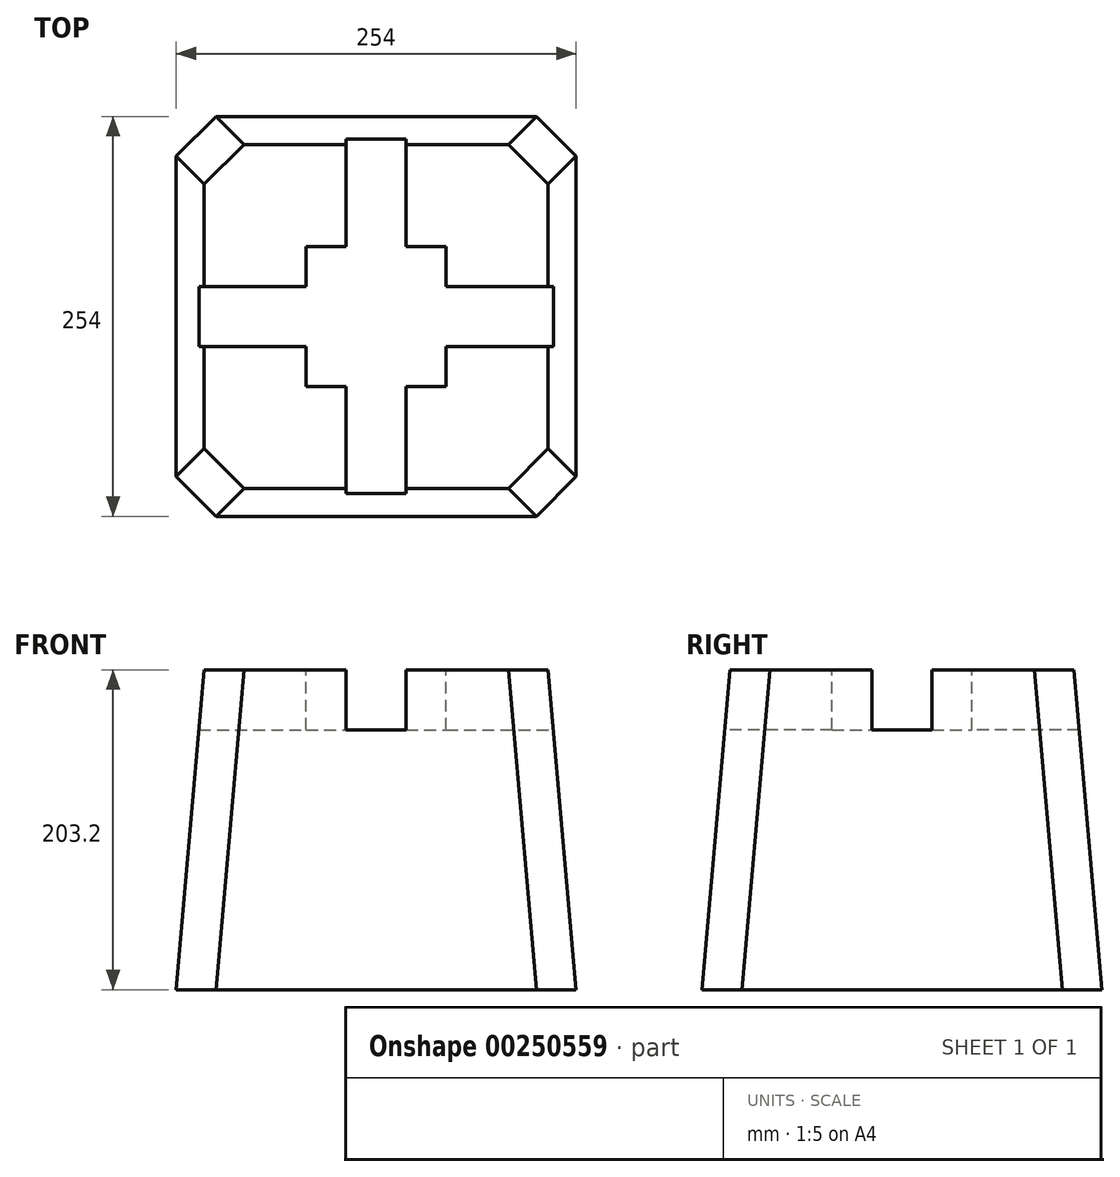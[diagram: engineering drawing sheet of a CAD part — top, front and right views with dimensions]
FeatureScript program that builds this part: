
annotation { "Feature Type Name" : "Feature", "Feature Type Description" : "" }
export const myFeature = defineFeature(function(context is Context, id is Id, definition is map)
    precondition{}
    {
        {
            var Q0;
            Q0=qCreatedBy(makeId("Top.planeOp"),FACE);
            var sketch = newSketch(context, id + "F0", { "sketchPlane" : qUnion([Q0])});
            skLineSegment(sketch, "E0.bottom", {"start": v(-127, -127) * mm, "end": v(127, -127) * mm});
            skLineSegment(sketch, "E0.top", {"start": v(-127, 127) * mm, "end": v(127, 127) * mm});
            skLineSegment(sketch, "E0.left", {"start": v(-127, -127) * mm, "end": v(-127, 127) * mm});
            skLineSegment(sketch, "E0.right", {"start": v(127, -127) * mm, "end": v(127, 127) * mm});
            skSolve(sketch);
        }
        {
            var Q0;
            Q0 = qSketchRegion(id + "F0", true);
            extrude(context, id + "F1", {"entities" : qUnion([Q0]), "depth" : 203.2 * mm, "hasDraft" : true, "draftAngle" : 5 * degree, "draftPullDirection" : true});
        }
        {
            var Q0;
            Q0=makeQuery(id+"F1.opExtrude","SWEPT_EDGE",EDGE,{"disambiguationData":[OSD([sQuery(id+"F0.wireOp",EDGE,"E0.bottom"),sQuery(id+"F0.wireOp",EDGE,"E0.left")])]});
            var Q1;
            Q1=makeQuery(id+"F1.opExtrude","SWEPT_EDGE",EDGE,{"disambiguationData":[OSD([sQuery(id+"F0.wireOp",EDGE,"E0.bottom"),sQuery(id+"F0.wireOp",EDGE,"E0.right")])]});
            var Q2;
            Q2=makeQuery(id+"F1.opExtrude","SWEPT_EDGE",EDGE,{"disambiguationData":[OSD([sQuery(id+"F0.wireOp",EDGE,"E0.top"),sQuery(id+"F0.wireOp",EDGE,"E0.right")])]});
            var Q3;
            Q3=makeQuery(id+"F1.opExtrude","SWEPT_EDGE",EDGE,{"disambiguationData":[OSD([sQuery(id+"F0.wireOp",EDGE,"E0.top"),sQuery(id+"F0.wireOp",EDGE,"E0.left")])]});
            chamfer(context, id + "F2", {"entities" : qUnion([Q0, Q1, Q2, Q3]), "width" : 25.4 * mm, "tangentPropagation" : true});
        }
        {
            var Q0;
            Q0=makeQuery(id+"F1.opExtrude","CAP_FACE",FACE,{"disambiguationData":[OSD([sQuery(id+"F0.wireOp",EDGE,"E0.bottom"),sQuery(id+"F0.wireOp",EDGE,"E0.top"),sQuery(id+"F0.wireOp",EDGE,"E0.left"),sQuery(id+"F0.wireOp",EDGE,"E0.right")])],"isStart":false});
            var sketch = newSketch(context, id + "F3", { "sketchPlane" : qUnion([Q0])});
            skLineSegment(sketch, "E1", {"start": v(0, 109.22) * mm, "end": v(0, -109.22) * mm, "construction": true});
            skLineSegment(sketch, "E2", {"start": v(-109.22, 0) * mm, "end": v(109.22, 0) * mm, "construction": true});
            skLineSegment(sketch, "E3.0", {"start": v(19.05, 132.02) * mm, "end": v(19.05, 44.45) * mm});
            skLineSegment(sketch, "E4.0", {"start": v(-19.05, 132.02) * mm, "end": v(-19.05, 44.45) * mm});
            skLineSegment(sketch, "E5.0", {"start": v(-137.83, -19.05) * mm, "end": v(-44.45, -19.05) * mm});
            skLineSegment(sketch, "E6.0", {"start": v(-137.83, 19.05) * mm, "end": v(-44.45, 19.05) * mm});
            skLineSegment(sketch, "E7.trimOffspring", {"start": v(-19.05, -44.45) * mm, "end": v(-19.05, -130.36) * mm});
            skLineSegment(sketch, "E8.trimOffspring", {"start": v(44.45, 19.05) * mm, "end": v(136.5, 19.05) * mm});
            skLineSegment(sketch, "E9.trimOffspring", {"start": v(19.05, -44.45) * mm, "end": v(19.05, -130.36) * mm});
            skLineSegment(sketch, "E10.trimOffspring", {"start": v(44.45, -19.05) * mm, "end": v(136.5, -19.05) * mm});
            skLineSegment(sketch, "E11.bottom", {"start": v(-44.45, -44.45) * mm, "end": v(-19.05, -44.45) * mm});
            skLineSegment(sketch, "E11.top", {"start": v(-44.45, 44.45) * mm, "end": v(-19.05, 44.45) * mm});
            skLineSegment(sketch, "E11.left", {"start": v(-44.45, -44.45) * mm, "end": v(-44.45, -19.05) * mm});
            skLineSegment(sketch, "E11.right", {"start": v(44.45, -44.45) * mm, "end": v(44.45, -19.05) * mm});
            skLineSegment(sketch, "E12.trimOffspring", {"start": v(19.05, 44.45) * mm, "end": v(44.45, 44.45) * mm});
            skLineSegment(sketch, "E13.trimOffspring", {"start": v(44.45, 19.05) * mm, "end": v(44.45, 44.45) * mm});
            skLineSegment(sketch, "E14.trimOffspring", {"start": v(19.05, -44.45) * mm, "end": v(44.45, -44.45) * mm});
            skLineSegment(sketch, "E15.trimOffspring", {"start": v(-44.45, 19.05) * mm, "end": v(-44.45, 44.45) * mm});
            skLineSegment(sketch, "E16", {"start": v(-19.05, -130.36) * mm, "end": v(19.05, -130.36) * mm});
            skLineSegment(sketch, "E17", {"start": v(-137.83, -19.05) * mm, "end": v(-137.83, 19.05) * mm});
            skLineSegment(sketch, "E18", {"start": v(-19.05, 132.02) * mm, "end": v(19.05, 132.02) * mm});
            skLineSegment(sketch, "E19", {"start": v(136.5, 19.05) * mm, "end": v(136.5, -19.05) * mm});
            skPoint(sketch, "E20.orphan", {"position": v(-19.05, 104.78) * mm});
            skPoint(sketch, "E21.orphan", {"position": v(19.05, 104.78) * mm});
            skPoint(sketch, "E22.orphan", {"position": v(104.78, 19.05) * mm});
            skPoint(sketch, "E23.orphan", {"position": v(19.05, -104.78) * mm});
            skPoint(sketch, "E24.orphan", {"position": v(-19.05, -104.78) * mm});
            skPoint(sketch, "E25.orphan", {"position": v(-104.78, -19.05) * mm});
            skPoint(sketch, "E26.orphan", {"position": v(-104.78, 19.05) * mm});
            skSolve(sketch);
        }
        {
            var Q0;
            Q0 = qSketchRegion(id + "F3", true);
            extrude(context, id + "F4", {"entities" : qUnion([Q0]), "operationType" : NewBodyOperationType.REMOVE, "oppositeDirection" : true, "depth" : 38.1 * mm});
        }
    });
